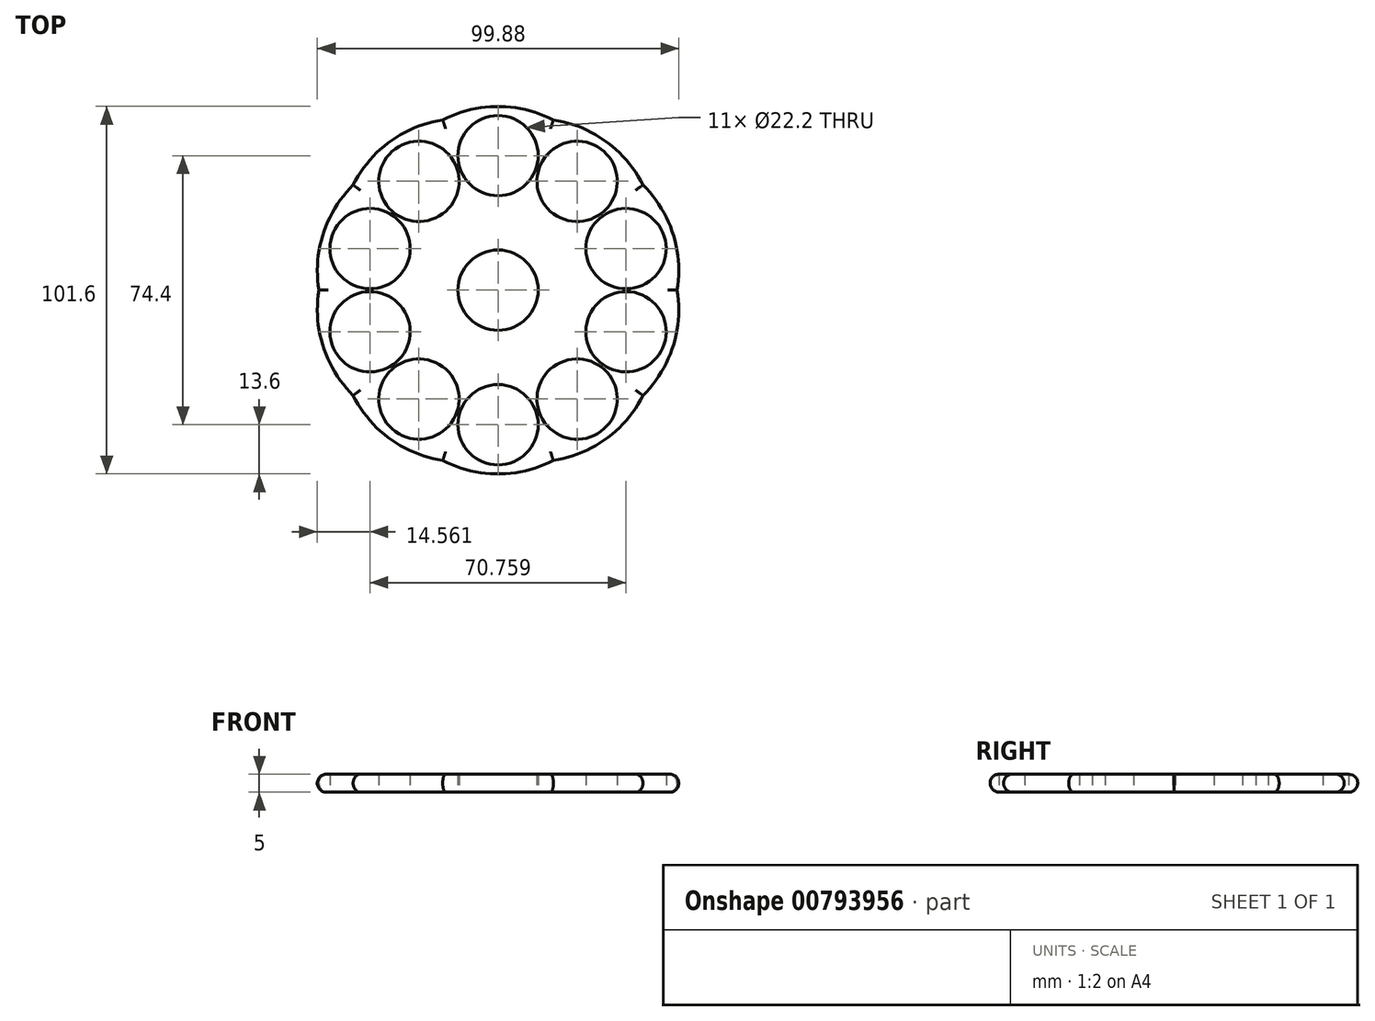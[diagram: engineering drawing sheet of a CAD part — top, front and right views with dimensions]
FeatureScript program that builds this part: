
annotation { "Feature Type Name" : "Feature", "Feature Type Description" : "" }
export const myFeature = defineFeature(function(context is Context, id is Id, definition is map)
    precondition{}
    {
        {
            var Q0;
            Q0=qCreatedBy(makeId("Top.planeOp"),FACE);
            var sketch = newSketch(context, id + "F0", { "sketchPlane" : qUnion([Q0])});
            skCircle(sketch, "E0", {"center": v(0, 0) * mm, "radius": 11.1 * mm});
            skCircle(sketch, "E1", {"center": v(0, 37.2) * mm, "radius": 11.1 * mm});
            skCircle(sketch, "E2.1.0", {"center": v(-21.87, 30.1) * mm, "radius": 11.1 * mm});
            skCircle(sketch, "E2.2.0", {"center": v(-35.38, 11.5) * mm, "radius": 11.1 * mm});
            skCircle(sketch, "E2.3.0", {"center": v(-35.38, -11.5) * mm, "radius": 11.1 * mm});
            skCircle(sketch, "E2.4.0", {"center": v(-21.87, -30.1) * mm, "radius": 11.1 * mm});
            skCircle(sketch, "E2.5.0", {"center": v(0, -37.2) * mm, "radius": 11.1 * mm});
            skCircle(sketch, "E2.6.0", {"center": v(21.87, -30.1) * mm, "radius": 11.1 * mm});
            skCircle(sketch, "E2.7.0", {"center": v(35.38, -11.5) * mm, "radius": 11.1 * mm});
            skCircle(sketch, "E2.8.0", {"center": v(35.38, 11.5) * mm, "radius": 11.1 * mm});
            skCircle(sketch, "E2.9.0", {"center": v(21.87, 30.1) * mm, "radius": 11.1 * mm});
            skLineSegment(sketch, "E3", {"start": v(0, 48.3) * mm, "end": v(0, 50.8) * mm});
            skLineSegment(sketch, "E4", {"start": v(-21.87, 30.1) * mm, "end": v(-21.87, 42.6) * mm});
            skLineSegment(sketch, "E5", {"start": v(21.87, 30.1) * mm, "end": v(21.87, 42.6) * mm});
            skArc(sketch, "E6", {"start": v(21.87, 42.6) * mm, "mid": v(0, 50.8) * mm, "end": v(-21.87, 42.6) * mm});
            skArc(sketch, "E7.1.0", {"start": v(-7.35, 47.31) * mm, "mid": v(-29.86, 41.1) * mm, "end": v(-42.73, 21.6) * mm});
            skArc(sketch, "E7.2.0", {"start": v(-33.75, 33.96) * mm, "mid": v(-48.31, 15.7) * mm, "end": v(-47.27, -7.63) * mm});
            skArc(sketch, "E7.3.0", {"start": v(-47.27, 7.63) * mm, "mid": v(-48.31, -15.7) * mm, "end": v(-33.75, -33.96) * mm});
            skArc(sketch, "E7.4.0", {"start": v(-42.73, -21.6) * mm, "mid": v(-29.86, -41.1) * mm, "end": v(-7.35, -47.31) * mm});
            skArc(sketch, "E7.5.0", {"start": v(-21.87, -42.6) * mm, "mid": v(0, -50.8) * mm, "end": v(21.87, -42.6) * mm});
            skArc(sketch, "E7.6.0", {"start": v(7.35, -47.31) * mm, "mid": v(29.86, -41.1) * mm, "end": v(42.73, -21.6) * mm});
            skArc(sketch, "E7.7.0", {"start": v(33.75, -33.96) * mm, "mid": v(48.31, -15.7) * mm, "end": v(47.27, 7.63) * mm});
            skArc(sketch, "E7.8.0", {"start": v(47.27, -7.63) * mm, "mid": v(48.31, 15.7) * mm, "end": v(33.75, 33.96) * mm});
            skArc(sketch, "E7.9.0", {"start": v(42.73, 21.6) * mm, "mid": v(29.86, 41.1) * mm, "end": v(7.35, 47.31) * mm});
            skSolve(sketch);
        }
        {
            var Q0;
            Q0 = qSketchRegion(id + "F0", true);
            extrude(context, id + "F1", {"entities" : qUnion([Q0]), "depth" : 5 * mm, "offsetDistance" : 25 * mm});
        }
        {
            var Q0;
            Q0=makeQuery(id+"F1.opExtrude","CAP_EDGE",EDGE,{"disambiguationData":[OSD([sQuery(id+"F0.wireOp",EDGE,"E7.4.0")])],"isStart":false});
            var Q1;
            Q1=makeQuery(id+"F1.opExtrude","CAP_EDGE",EDGE,{"disambiguationData":[OSD([sQuery(id+"F0.wireOp",EDGE,"E7.3.0")])],"isStart":false});
            var Q2;
            Q2=makeQuery(id+"F1.opExtrude","CAP_EDGE",EDGE,{"disambiguationData":[OSD([sQuery(id+"F0.wireOp",EDGE,"E7.5.0")])],"isStart":false});
            var Q3;
            Q3=makeQuery(id+"F1.opExtrude","CAP_EDGE",EDGE,{"disambiguationData":[OSD([sQuery(id+"F0.wireOp",EDGE,"E7.6.0")])],"isStart":false});
            var Q4;
            Q4=makeQuery(id+"F1.opExtrude","CAP_EDGE",EDGE,{"disambiguationData":[OSD([sQuery(id+"F0.wireOp",EDGE,"E7.7.0")])],"isStart":false});
            var Q5;
            Q5=makeQuery(id+"F1.opExtrude","CAP_EDGE",EDGE,{"disambiguationData":[OSD([sQuery(id+"F0.wireOp",EDGE,"E7.8.0")])],"isStart":false});
            var Q6;
            Q6=makeQuery(id+"F1.opExtrude","CAP_EDGE",EDGE,{"disambiguationData":[OSD([sQuery(id+"F0.wireOp",EDGE,"E7.9.0")])],"isStart":false});
            var Q7;
            Q7=makeQuery(id+"F1.opExtrude","CAP_EDGE",EDGE,{"disambiguationData":[OSD([sQuery(id+"F0.wireOp",EDGE,"E6")])],"isStart":false});
            var Q8;
            Q8=makeQuery(id+"F1.opExtrude","CAP_EDGE",EDGE,{"disambiguationData":[OSD([sQuery(id+"F0.wireOp",EDGE,"E7.1.0")])],"isStart":false});
            var Q9;
            Q9=makeQuery(id+"F1.opExtrude","CAP_EDGE",EDGE,{"disambiguationData":[OSD([sQuery(id+"F0.wireOp",EDGE,"E7.2.0")])],"isStart":false});
            var Q10;
            Q10=makeQuery(id+"F1.opExtrude","CAP_EDGE",EDGE,{"disambiguationData":[OSD([sQuery(id+"F0.wireOp",EDGE,"E7.4.0")])],"isStart":true});
            var Q11;
            Q11=makeQuery(id+"F1.opExtrude","CAP_EDGE",EDGE,{"disambiguationData":[OSD([sQuery(id+"F0.wireOp",EDGE,"E7.5.0")])],"isStart":true});
            var Q12;
            Q12=makeQuery(id+"F1.opExtrude","CAP_EDGE",EDGE,{"disambiguationData":[OSD([sQuery(id+"F0.wireOp",EDGE,"E7.6.0")])],"isStart":true});
            var Q13;
            Q13=makeQuery(id+"F1.opExtrude","CAP_EDGE",EDGE,{"disambiguationData":[OSD([sQuery(id+"F0.wireOp",EDGE,"E7.7.0")])],"isStart":true});
            var Q14;
            Q14=makeQuery(id+"F1.opExtrude","CAP_EDGE",EDGE,{"disambiguationData":[OSD([sQuery(id+"F0.wireOp",EDGE,"E7.8.0")])],"isStart":true});
            var Q15;
            Q15=makeQuery(id+"F1.opExtrude","CAP_EDGE",EDGE,{"disambiguationData":[OSD([sQuery(id+"F0.wireOp",EDGE,"E7.9.0")])],"isStart":true});
            var Q16;
            Q16=makeQuery(id+"F1.opExtrude","CAP_EDGE",EDGE,{"disambiguationData":[OSD([sQuery(id+"F0.wireOp",EDGE,"E6")])],"isStart":true});
            var Q17;
            Q17=makeQuery(id+"F1.opExtrude","CAP_EDGE",EDGE,{"disambiguationData":[OSD([sQuery(id+"F0.wireOp",EDGE,"E7.1.0")])],"isStart":true});
            var Q18;
            Q18=makeQuery(id+"F1.opExtrude","CAP_EDGE",EDGE,{"disambiguationData":[OSD([sQuery(id+"F0.wireOp",EDGE,"E7.2.0")])],"isStart":true});
            var Q19;
            Q19=makeQuery(id+"F1.opExtrude","CAP_EDGE",EDGE,{"disambiguationData":[OSD([sQuery(id+"F0.wireOp",EDGE,"E7.3.0")])],"isStart":true});
            fillet(context, id + "F2", {"entities" : qUnion([Q0, Q1, Q2, Q3, Q4, Q5, Q6, Q7, Q8, Q9, Q10, Q11, Q12, Q13, Q14, Q15, Q16, Q17, Q18, Q19]), "radius" : 2.5 * mm, "tangentPropagation" : true, "allowEdgeOverflow" : false});
        }
    });
